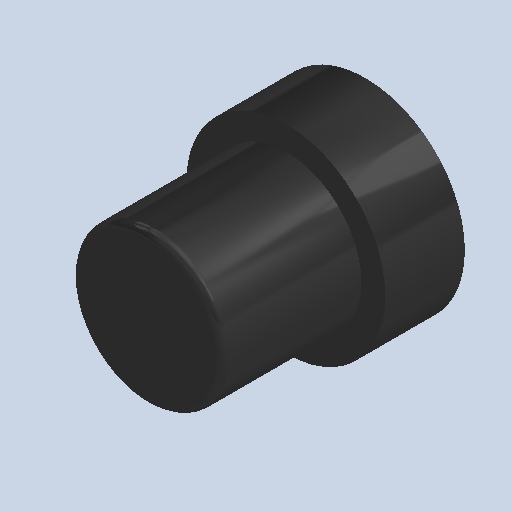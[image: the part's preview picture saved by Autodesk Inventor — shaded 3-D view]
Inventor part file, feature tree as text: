
AUTODESK INVENTOR PART (.ipt)
format: ipt  version: 2022.1 (Build 261234000, 234)  size: 94,720 bytes
history: mixed  units: mm (DEFAULTED — no unit token found)
features: other x8, fillet x1, imported_body x1
bodies: Body1 (imported_parasolid)
feature tree (10):
  other  "Sólido1"
  other  "Origen"
  other  "Plano YZ"
  other  "Plano XZ"
  other  "Plano XY"
  other  "Eje X"
  other  "Eje Y"
  other  "Eje Z"
  fillet  "Fillet1"  [1 undecoded]
  imported_body  NMx_Import_Brep_tag  [imported B-rep: ~6 faces, bbox_mm=[0.8, 0.0, 5.5]]
note: 1 required parameter value undecoded (feature->parameter linkage not recoverable at this tier; creation-order binding heuristic only, values carry confidence <= 0.55)
